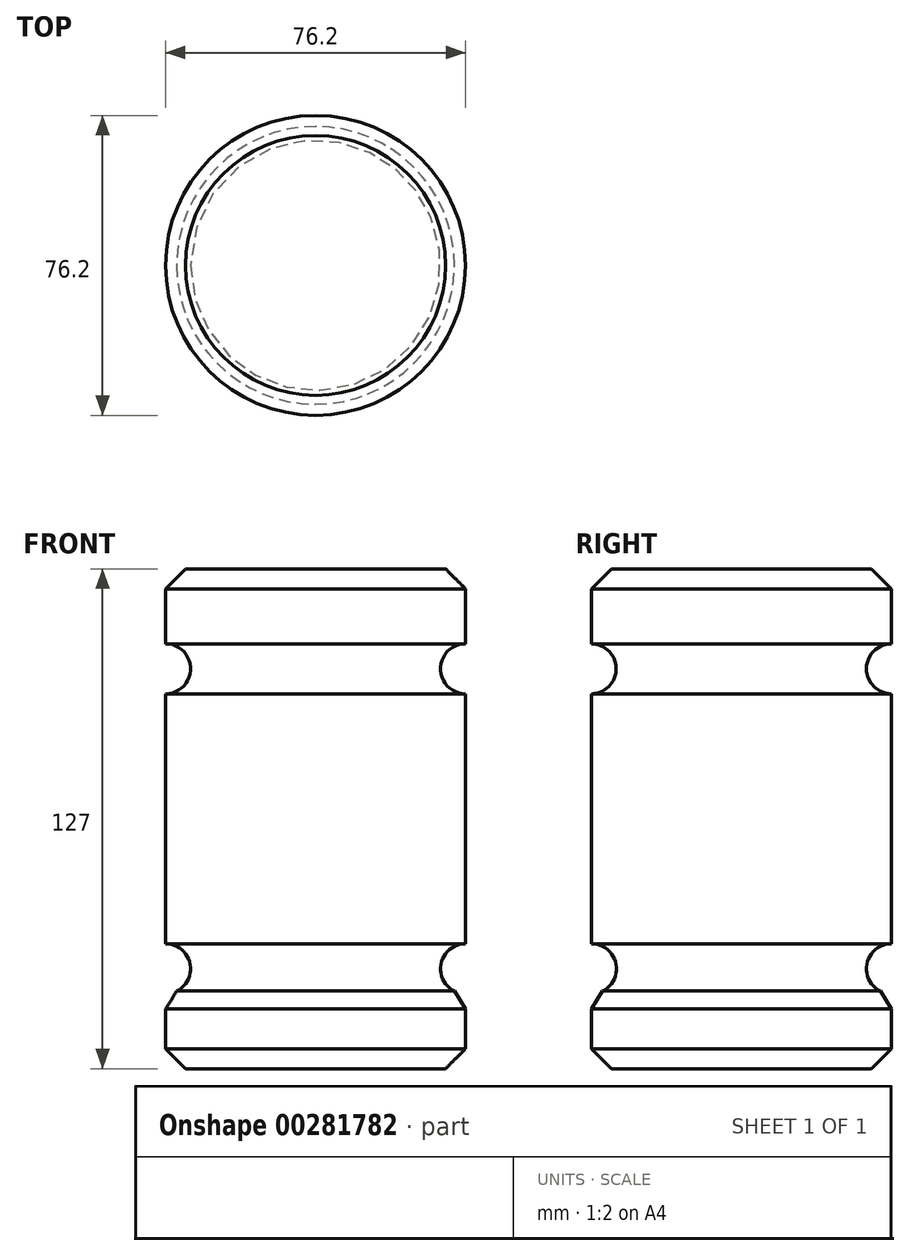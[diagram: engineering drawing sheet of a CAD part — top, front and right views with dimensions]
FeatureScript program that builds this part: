
annotation { "Feature Type Name" : "Feature", "Feature Type Description" : "" }
export const myFeature = defineFeature(function(context is Context, id is Id, definition is map)
    precondition{}
    {
        {
            var Q0;
            Q0=qCreatedBy(makeId("Front.planeOp"),FACE);
            var sketch = newSketch(context, id + "F0", { "sketchPlane" : qUnion([Q0])});
            skLineSegment(sketch, "E0.bottom", {"start": v(0, 0) * mm, "end": v(-38.1, 0) * mm});
            skLineSegment(sketch, "E0.top", {"start": v(0, 127) * mm, "end": v(-38.1, 127) * mm});
            skLineSegment(sketch, "E0.left", {"start": v(0, 0) * mm, "end": v(0, 19.05) * mm});
            skLineSegment(sketch, "E0.right", {"start": v(-38.1, 0) * mm, "end": v(-38.1, 127) * mm});
            skArc(sketch, "E1", {"start": v(0, 107.95) * mm, "mid": v(-6.35, 101.6) * mm, "end": v(0, 95.25) * mm});
            skArc(sketch, "E2", {"start": v(0, 31.75) * mm, "mid": v(-6.35, 25.4) * mm, "end": v(0, 19.05) * mm});
            skLineSegment(sketch, "E3.trimOffspring", {"start": v(0, 31.75) * mm, "end": v(0, 95.25) * mm});
            skLineSegment(sketch, "E4.trimOffspring", {"start": v(0, 107.95) * mm, "end": v(0, 127) * mm});
            skSolve(sketch);
        }
        {
            var Q0;
            Q0 = qSketchRegion(id + "F0", true);
            var Q1;
            Q1=sQuery(id+"F0.wireOp",EDGE,"E0.right");
            revolve(context, id + "F1", {"entities" : qUnion([Q0]), "axis" : qUnion([Q1]), "revolveType" : RevolveType.FULL});
        }
        {
            var Q0;
            Q0=makeQuery(id+"F1.opRevolve","SWEPT_EDGE",EDGE,{"disambiguationData":[OSD([sQuery(id+"F0.wireOp",EDGE,"E0.top"),sQuery(id+"F0.wireOp",EDGE,"E4.trimOffspring")])]});
            var Q1;
            Q1=makeQuery(id+"F1.opRevolve","SWEPT_FACE",FACE,{"disambiguationData":[OSD([sQuery(id+"F0.wireOp",EDGE,"E0.left")])]});
            chamfer(context, id + "F2", {"entities" : qUnion([Q0, Q1]), "width" : 5.08 * mm, "tangentPropagation" : true});
        }
    });
